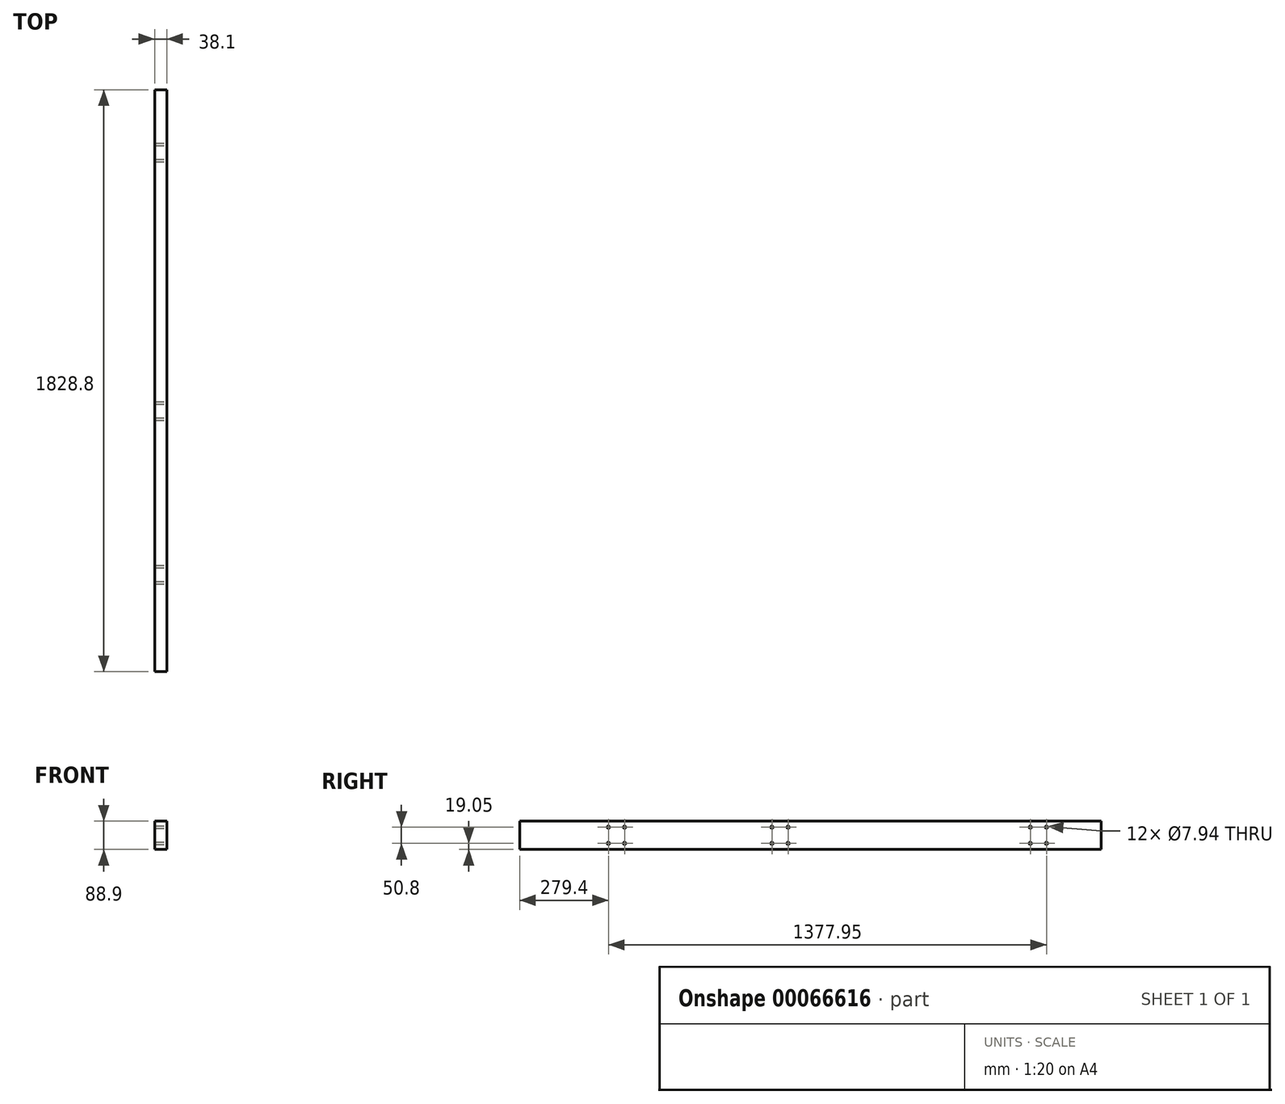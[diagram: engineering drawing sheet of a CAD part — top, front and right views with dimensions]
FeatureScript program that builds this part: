
annotation { "Feature Type Name" : "Feature", "Feature Type Description" : "" }
export const myFeature = defineFeature(function(context is Context, id is Id, definition is map)
    precondition{}
    {
        {
            var Q0;
            Q0=qCreatedBy(makeId("Front.planeOp"),FACE);
            var sketch = newSketch(context, id + "F0", { "sketchPlane" : qUnion([Q0])});
            skLineSegment(sketch, "E0.rect.bottom", {"start": v(19.05, 44.45) * mm, "end": v(-19.05, 44.45) * mm});
            skLineSegment(sketch, "E0.rect.top", {"start": v(19.05, -44.45) * mm, "end": v(-19.05, -44.45) * mm});
            skLineSegment(sketch, "E0.rect.left", {"start": v(19.05, 44.45) * mm, "end": v(19.05, -44.45) * mm});
            skLineSegment(sketch, "E0.rect.right", {"start": v(-19.05, 44.45) * mm, "end": v(-19.05, -44.45) * mm});
            skPoint(sketch, "E0.rect.middle", {"position": v(0, 0) * mm});
            skSolve(sketch);
        }
        {
            var Q0;
            Q0=qSketchRegion(id+"F0",true);
            extrude(context, id + "F1", {"entities" : qUnion([Q0]), "depth" : 1828.8 * mm});
        }
        {
            var Q0;
            Q0=makeQuery(id+"F1.opExtrude","SWEPT_FACE",FACE,{"disambiguationData":[OSD([sQuery(id+"F0.wireOp",EDGE,"E0.rect.left")])]});
            var sketch = newSketch(context, id + "F2", { "sketchPlane" : qUnion([Q0])});
            skLineSegment(sketch, "E1.rect.bottom", {"start": v(-965.2, 44.45) * mm, "end": v(-1054.1, 44.45) * mm, "construction": true});
            skLineSegment(sketch, "E1.rect.top", {"start": v(-965.2, -44.45) * mm, "end": v(-1054.1, -44.45) * mm, "construction": true});
            skLineSegment(sketch, "E1.rect.left", {"start": v(-965.2, 44.45) * mm, "end": v(-965.2, -44.45) * mm, "construction": true});
            skLineSegment(sketch, "E1.rect.right", {"start": v(-1054.1, 44.45) * mm, "end": v(-1054.1, -44.45) * mm, "construction": true});
            skPoint(sketch, "E1.rect.middle", {"position": v(-1009.65, 0) * mm});
            skLineSegment(sketch, "E2.rect.bottom", {"start": v(-1479.55, -44.45) * mm, "end": v(-1568.45, -44.45) * mm, "construction": true});
            skLineSegment(sketch, "E2.rect.top", {"start": v(-1479.55, 44.45) * mm, "end": v(-1568.45, 44.45) * mm, "construction": true});
            skLineSegment(sketch, "E2.rect.left", {"start": v(-1479.55, -44.45) * mm, "end": v(-1479.55, 44.45) * mm, "construction": true});
            skLineSegment(sketch, "E2.rect.right", {"start": v(-1568.45, -44.45) * mm, "end": v(-1568.45, 44.45) * mm, "construction": true});
            skPoint(sketch, "E2.rect.middle", {"position": v(-1524, 0) * mm});
            skLineSegment(sketch, "E3.rect.bottom", {"start": v(-1035.05, -25.4) * mm, "end": v(-984.25, -25.4) * mm, "construction": true});
            skLineSegment(sketch, "E3.rect.top", {"start": v(-1035.05, 25.4) * mm, "end": v(-984.25, 25.4) * mm, "construction": true});
            skLineSegment(sketch, "E3.rect.left", {"start": v(-1035.05, -25.4) * mm, "end": v(-1035.05, 25.4) * mm, "construction": true});
            skLineSegment(sketch, "E3.rect.right", {"start": v(-984.25, -25.4) * mm, "end": v(-984.25, 25.4) * mm, "construction": true});
            skLineSegment(sketch, "E4.rect.bottom", {"start": v(-1498.6, -25.4) * mm, "end": v(-1549.4, -25.4) * mm, "construction": true});
            skLineSegment(sketch, "E4.rect.top", {"start": v(-1498.6, 25.4) * mm, "end": v(-1549.4, 25.4) * mm, "construction": true});
            skLineSegment(sketch, "E4.rect.left", {"start": v(-1498.6, -25.4) * mm, "end": v(-1498.6, 25.4) * mm, "construction": true});
            skLineSegment(sketch, "E4.rect.right", {"start": v(-1549.4, -25.4) * mm, "end": v(-1549.4, 25.4) * mm, "construction": true});
            skCircle(sketch, "E5", {"center": v(-1498.6, 25.4) * mm, "radius": 3.97 * mm});
            skCircle(sketch, "E6", {"center": v(-1498.6, -25.4) * mm, "radius": 3.97 * mm});
            skCircle(sketch, "E7", {"center": v(-1549.4, -25.4) * mm, "radius": 3.97 * mm});
            skCircle(sketch, "E8", {"center": v(-1549.4, 25.4) * mm, "radius": 3.97 * mm});
            skCircle(sketch, "E9", {"center": v(-1035.05, 25.4) * mm, "radius": 3.97 * mm});
            skCircle(sketch, "E10", {"center": v(-1035.05, -25.4) * mm, "radius": 3.97 * mm});
            skCircle(sketch, "E11", {"center": v(-984.25, -25.4) * mm, "radius": 3.97 * mm});
            skCircle(sketch, "E12", {"center": v(-984.25, 25.4) * mm, "radius": 3.97 * mm});
            skLineSegment(sketch, "E13.rect.bottom", {"start": v(-152.4, 44.45) * mm, "end": v(-241.3, 44.45) * mm, "construction": true});
            skLineSegment(sketch, "E13.rect.top", {"start": v(-152.4, -44.45) * mm, "end": v(-241.3, -44.45) * mm, "construction": true});
            skLineSegment(sketch, "E13.rect.left", {"start": v(-152.4, 44.45) * mm, "end": v(-152.4, -44.45) * mm, "construction": true});
            skLineSegment(sketch, "E13.rect.right", {"start": v(-241.3, 44.45) * mm, "end": v(-241.3, -44.45) * mm, "construction": true});
            skPoint(sketch, "E13.rect.middle", {"position": v(-196.85, 0) * mm});
            skLineSegment(sketch, "E14.rect.bottom", {"start": v(-171.45, -25.4) * mm, "end": v(-222.25, -25.4) * mm, "construction": true});
            skLineSegment(sketch, "E14.rect.top", {"start": v(-171.45, 25.4) * mm, "end": v(-222.25, 25.4) * mm, "construction": true});
            skLineSegment(sketch, "E14.rect.left", {"start": v(-171.45, -25.4) * mm, "end": v(-171.45, 25.4) * mm, "construction": true});
            skLineSegment(sketch, "E14.rect.right", {"start": v(-222.25, -25.4) * mm, "end": v(-222.25, 25.4) * mm, "construction": true});
            skCircle(sketch, "E15", {"center": v(-222.25, 25.4) * mm, "radius": 3.97 * mm});
            skCircle(sketch, "E16", {"center": v(-171.45, 25.4) * mm, "radius": 3.97 * mm});
            skCircle(sketch, "E17", {"center": v(-171.45, -25.4) * mm, "radius": 3.97 * mm});
            skCircle(sketch, "E18", {"center": v(-222.25, -25.4) * mm, "radius": 3.97 * mm});
            skSolve(sketch);
        }
        {
            var Q0;
            Q0=qSketchRegion(id+"F2",true);
            extrude(context, id + "F3", {"entities" : qUnion([Q0]), "operationType" : NewBodyOperationType.REMOVE, "endBound" : BoundingType.THROUGH_ALL, "oppositeDirection" : true, "depth" : 25.4 * mm});
        }
    });
